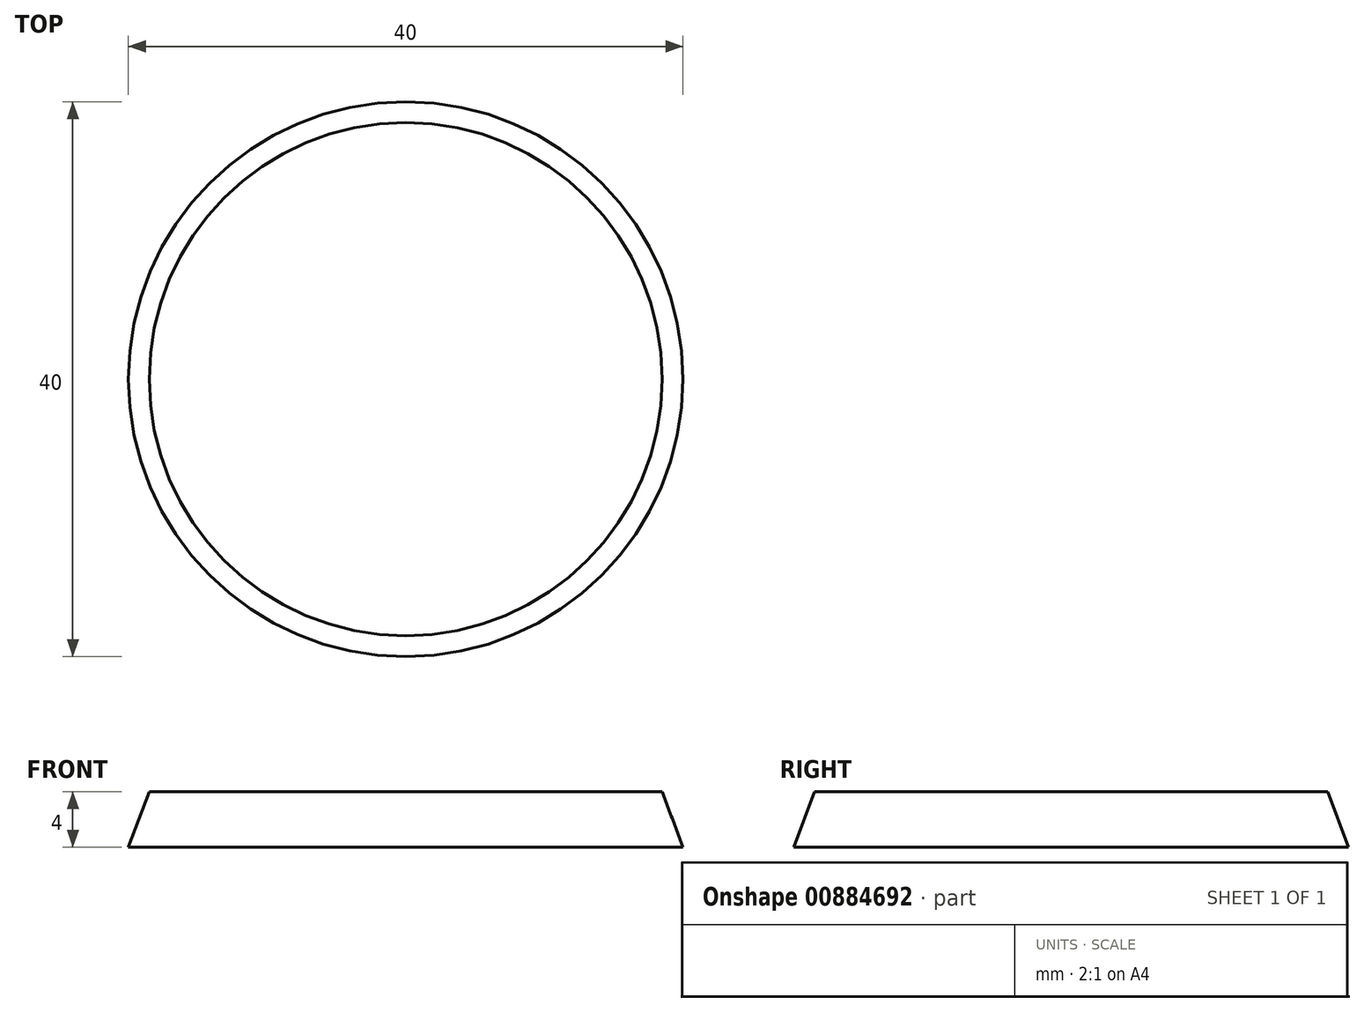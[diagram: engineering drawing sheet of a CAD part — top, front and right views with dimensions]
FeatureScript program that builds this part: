
annotation { "Feature Type Name" : "Feature", "Feature Type Description" : "" }
export const myFeature = defineFeature(function(context is Context, id is Id, definition is map)
    precondition{}
    {
        {
            var Q0;
            Q0=qCreatedBy(makeId("Top.planeOp"),FACE);
            var sketch = newSketch(context, id + "F0", { "sketchPlane" : qUnion([Q0])});
            skCircle(sketch, "E0", {"center": v(0, 0) * mm, "radius": 20 * mm});
            skSolve(sketch);
        }
        {
            var Q0;
            Q0=makeQuery(id+"F0.imprint","IMPRINT",FACE,{"disambiguationData":[TD([[makeQuery(id+"F0.imprint","IMPRINT",EDGE,{"derivedFrom":sQuery(id+"F0.wireOp",EDGE,"E0")}),1.0]])]});
            cPlane(context, id + "F1", {"entities" : qUnion([Q0]), "cplaneType" : CPlaneType.OFFSET, "offset" : 4 * mm, "width" : 150 * mm, "height" : 150 * mm});
        }
        {
            var Q0;
            Q0=qCreatedBy(id+"F1.planeOp",FACE);
            var sketch = newSketch(context, id + "F2", { "sketchPlane" : qUnion([Q0])});
            skCircle(sketch, "E1", {"center": v(0, 0) * mm, "radius": 18.5 * mm});
            skSolve(sketch);
        }
        {
            var Q0;
            Q0=makeQuery(id+"F0.imprint","IMPRINT",FACE,{"disambiguationData":[TD([[makeQuery(id+"F0.imprint","IMPRINT",EDGE,{"derivedFrom":sQuery(id+"F0.wireOp",EDGE,"E0")}),1.0]])]});
            var Q1;
            Q1=makeQuery(id+"F2.imprint","IMPRINT",FACE,{"disambiguationData":[TD([[makeQuery(id+"F2.imprint","IMPRINT",EDGE,{"derivedFrom":sQuery(id+"F2.wireOp",EDGE,"E1")}),1.0]])]});
            loft(context, id + "F3", {"sheetProfilesArray" : [{ "sheetProfileEntities" : qUnion([Q0]) }, { "sheetProfileEntities" : qUnion([Q1]) }]});
        }
    });
